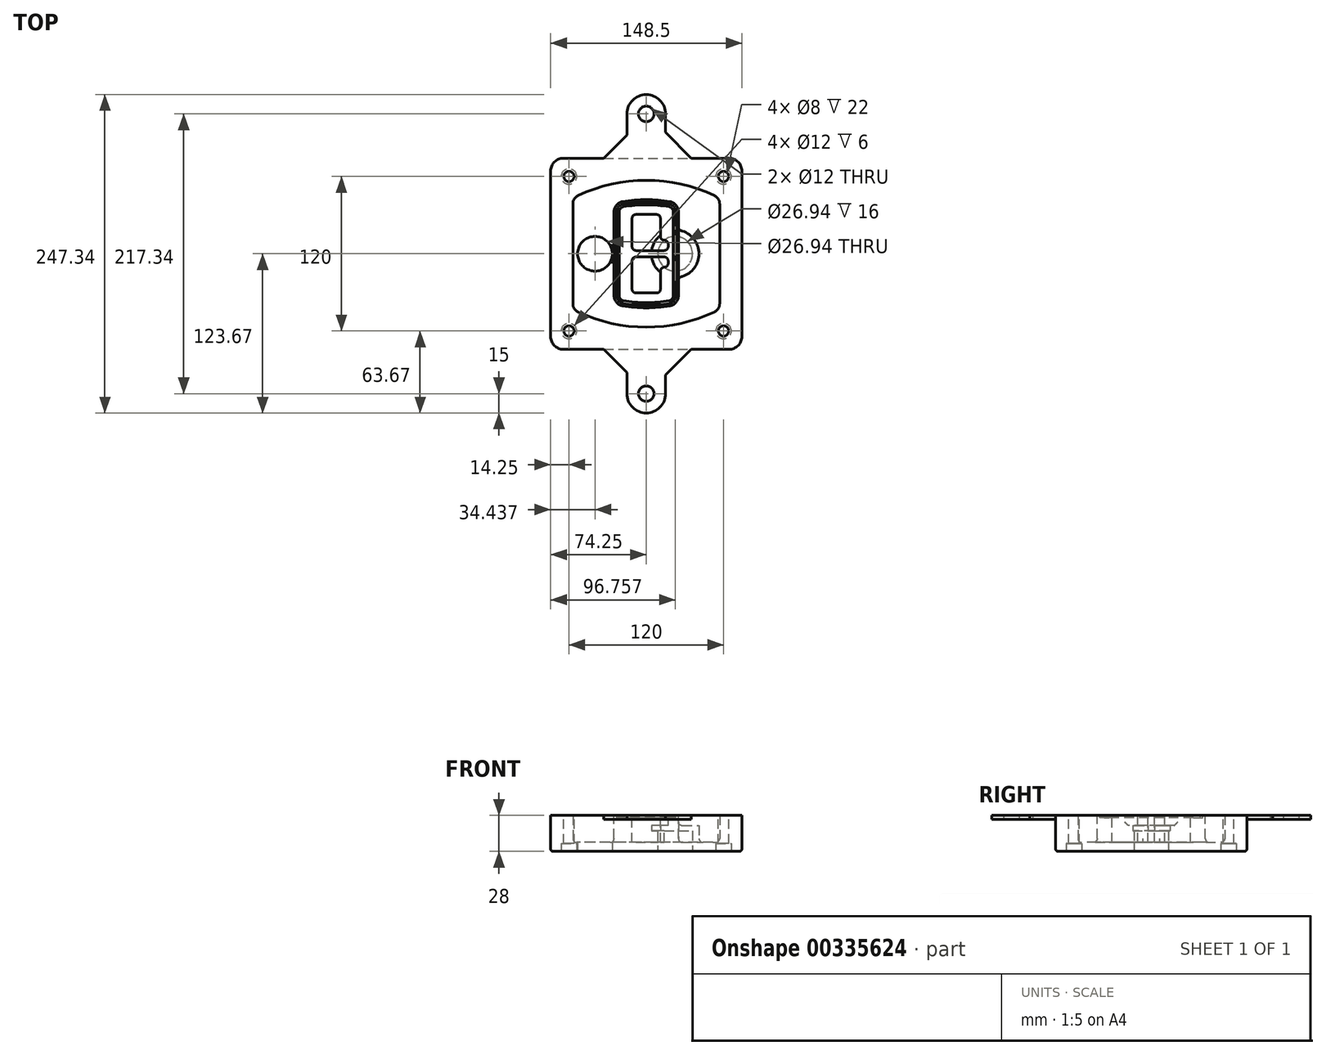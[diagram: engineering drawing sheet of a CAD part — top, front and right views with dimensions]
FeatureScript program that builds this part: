
annotation { "Feature Type Name" : "Feature", "Feature Type Description" : "" }
export const myFeature = defineFeature(function(context is Context, id is Id, definition is map)
    precondition{}
    {
        {
            var Q0;
            Q0=qCreatedBy(makeId("Top.planeOp"),FACE);
            var sketch = newSketch(context, id + "F0", { "sketchPlane" : qUnion([Q0])});
            skPoint(sketch, "E0.rect.middle", {"position": v(0, 0) * mm});
            skLineSegment(sketch, "E1.bottom", {"start": v(-64.25, -74.25) * mm, "end": v(64.25, -74.25) * mm});
            skLineSegment(sketch, "E1.top", {"start": v(-64.25, 74.25) * mm, "end": v(64.25, 74.25) * mm});
            skLineSegment(sketch, "E1.left", {"start": v(-74.25, -64.25) * mm, "end": v(-74.25, 64.25) * mm});
            skLineSegment(sketch, "E1.right", {"start": v(74.25, -64.25) * mm, "end": v(74.25, 64.25) * mm});
            skLineSegment(sketch, "E2", {"start": v(-74.25, 74.25) * mm, "end": v(74.25, -74.25) * mm, "construction": true});
            skLineSegment(sketch, "E3", {"start": v(74.25, 74.25) * mm, "end": v(-74.25, -74.25) * mm, "construction": true});
            skCircle(sketch, "E4", {"center": v(-60, 60) * mm, "radius": 4 * mm});
            skCircle(sketch, "E5", {"center": v(60, 60) * mm, "radius": 4 * mm});
            skCircle(sketch, "E6", {"center": v(60, -60) * mm, "radius": 4 * mm});
            skCircle(sketch, "E7", {"center": v(-60, -60) * mm, "radius": 4 * mm});
            skLineSegment(sketch, "E8", {"start": v(-60, 60) * mm, "end": v(60, 60) * mm, "construction": true});
            skLineSegment(sketch, "E9", {"start": v(60, 60) * mm, "end": v(60, -60) * mm, "construction": true});
            skLineSegment(sketch, "E10", {"start": v(60, -60) * mm, "end": v(-60, -60) * mm, "construction": true});
            skLineSegment(sketch, "E11", {"start": v(-60, -60) * mm, "end": v(-60, 60) * mm, "construction": true});
            skLineSegment(sketch, "E12", {"start": v(-60, 38.83) * mm, "end": v(-60, -38.83) * mm});
            skLineSegment(sketch, "E13", {"start": v(60, 38.83) * mm, "end": v(60, -38.83) * mm});
            skArc(sketch, "E14", {"start": v(54.26, 47.88) * mm, "mid": v(0, 60) * mm, "end": v(-54.26, 47.88) * mm});
            skArc(sketch, "E15", {"start": v(-54.26, -47.88) * mm, "mid": v(0, -60) * mm, "end": v(54.26, -47.88) * mm});
            skLineSegment(sketch, "E16", {"start": v(-60, 0) * mm, "end": v(60, 0) * mm, "construction": true});
            skPoint(sketch, "E17.visualSharp", {"position": v(-60, -45) * mm});
            skArc(sketch, "E17.filletArc", {"start": v(-60, -38.83) * mm, "mid": v(-58.44, -44.2) * mm, "end": v(-54.26, -47.88) * mm});
            skPoint(sketch, "E18.visualSharp", {"position": v(-60, 45) * mm});
            skArc(sketch, "E18.filletArc", {"start": v(-54.26, 47.88) * mm, "mid": v(-58.44, 44.2) * mm, "end": v(-60, 38.83) * mm});
            skPoint(sketch, "E19.visualSharp", {"position": v(60, 45) * mm});
            skArc(sketch, "E19.filletArc", {"start": v(60, 38.83) * mm, "mid": v(58.44, 44.2) * mm, "end": v(54.26, 47.88) * mm});
            skPoint(sketch, "E20.visualSharp", {"position": v(60, -45) * mm});
            skArc(sketch, "E20.filletArc", {"start": v(54.26, -47.88) * mm, "mid": v(58.44, -44.2) * mm, "end": v(60, -38.83) * mm});
            skPoint(sketch, "E21.visualSharp", {"position": v(-74.25, 74.25) * mm});
            skArc(sketch, "E21.filletArc", {"start": v(-64.25, 74.25) * mm, "mid": v(-71.32, 71.32) * mm, "end": v(-74.25, 64.25) * mm});
            skPoint(sketch, "E22.visualSharp", {"position": v(74.25, 74.25) * mm});
            skArc(sketch, "E22.filletArc", {"start": v(74.25, 64.25) * mm, "mid": v(71.32, 71.32) * mm, "end": v(64.25, 74.25) * mm});
            skPoint(sketch, "E23.visualSharp", {"position": v(74.25, -74.25) * mm});
            skArc(sketch, "E23.filletArc", {"start": v(64.25, -74.25) * mm, "mid": v(71.32, -71.32) * mm, "end": v(74.25, -64.25) * mm});
            skPoint(sketch, "E24.visualSharp", {"position": v(-74.25, -74.25) * mm});
            skArc(sketch, "E24.filletArc", {"start": v(-74.25, -64.25) * mm, "mid": v(-71.32, -71.32) * mm, "end": v(-64.25, -74.25) * mm});
            skArc(sketch, "E25.0", {"start": v(57, 38.83) * mm, "mid": v(55.9, 42.58) * mm, "end": v(52.98, 45.17) * mm});
            skLineSegment(sketch, "E25.1", {"start": v(57, 38.83) * mm, "end": v(57, -38.83) * mm});
            skArc(sketch, "E25.2", {"start": v(52.98, -45.17) * mm, "mid": v(55.9, -42.58) * mm, "end": v(57, -38.83) * mm});
            skArc(sketch, "E25.3", {"start": v(-52.98, -45.17) * mm, "mid": v(0, -57) * mm, "end": v(52.98, -45.17) * mm});
            skArc(sketch, "E25.4", {"start": v(-57, -38.83) * mm, "mid": v(-55.9, -42.58) * mm, "end": v(-52.98, -45.17) * mm});
            skArc(sketch, "E25.5", {"start": v(52.98, 45.17) * mm, "mid": v(0, 57) * mm, "end": v(-52.98, 45.17) * mm});
            skLineSegment(sketch, "E25.6", {"start": v(-57, 38.83) * mm, "end": v(-57, -38.83) * mm});
            skArc(sketch, "E25.7", {"start": v(-52.98, 45.17) * mm, "mid": v(-55.9, 42.58) * mm, "end": v(-57, 38.83) * mm});
            skArc(sketch, "E26.0", {"start": v(-55.96, 51.5) * mm, "mid": v(-61.82, 46.33) * mm, "end": v(-64, 38.83) * mm});
            skArc(sketch, "E26.1", {"start": v(55.96, 51.5) * mm, "mid": v(0, 64) * mm, "end": v(-55.96, 51.5) * mm});
            skArc(sketch, "E26.2", {"start": v(64, 38.83) * mm, "mid": v(61.82, 46.33) * mm, "end": v(55.96, 51.5) * mm});
            skLineSegment(sketch, "E26.3", {"start": v(64, 38.83) * mm, "end": v(64, -38.83) * mm});
            skArc(sketch, "E26.4", {"start": v(55.96, -51.5) * mm, "mid": v(61.82, -46.33) * mm, "end": v(64, -38.83) * mm});
            skLineSegment(sketch, "E26.5", {"start": v(-64, 38.83) * mm, "end": v(-64, -38.83) * mm});
            skArc(sketch, "E26.6", {"start": v(-55.96, -51.5) * mm, "mid": v(0, -64) * mm, "end": v(55.96, -51.5) * mm});
            skArc(sketch, "E26.7", {"start": v(-64, -38.83) * mm, "mid": v(-61.82, -46.33) * mm, "end": v(-55.96, -51.5) * mm});
            skSolve(sketch);
        }
        {
            var Q0;
            Q0=makeQuery(id+"F0.imprint","IMPRINT",FACE,{"disambiguationData":[TD([[makeQuery(id+"F0.imprint","IMPRINT",EDGE,{"derivedFrom":sQuery(id+"F0.wireOp",EDGE,"E1.bottom")}),1.0]])]});
            var Q1;
            Q1=makeQuery(id+"F0.imprint","IMPRINT",FACE,{"disambiguationData":[TD([[makeQuery(id+"F0.imprint","IMPRINT",EDGE,{"derivedFrom":sQuery(id+"F0.wireOp",EDGE,"E12")}),1.0]])]});
            var Q2;
            Q2=makeQuery(id+"F0.imprint","IMPRINT",FACE,{"disambiguationData":[TD([[makeQuery(id+"F0.imprint","IMPRINT",EDGE,{"derivedFrom":sQuery(id+"F0.wireOp",EDGE,"E25.0")}),1.0]])]});
            var Q3;
            Q3=makeQuery(id+"F0.imprint","IMPRINT",FACE,{"disambiguationData":[TD([[makeQuery(id+"F0.imprint","IMPRINT",EDGE,{"derivedFrom":sQuery(id+"F0.wireOp",EDGE,"E12")}),-1.0]])]});
            extrude(context, id + "F1", {"entities" : qUnion([Q0, Q1, Q2, Q3]), "oppositeDirection" : true, "depth" : 25 * mm});
        }
        {
            var Q0;
            Q0=makeQuery(id+"F0.imprint","IMPRINT",FACE,{"disambiguationData":[TD([[makeQuery(id+"F0.imprint","IMPRINT",EDGE,{"derivedFrom":sQuery(id+"F0.wireOp",EDGE,"E12")}),1.0]])]});
            extrude(context, id + "F2", {"entities" : qUnion([Q0]), "operationType" : NewBodyOperationType.ADD, "depth" : 3 * mm});
        }
        {
            var Q0;
            Q0=makeQuery(id+"F0.imprint","IMPRINT",FACE,{"disambiguationData":[TD([[makeQuery(id+"F0.imprint","IMPRINT",EDGE,{"derivedFrom":sQuery(id+"F0.wireOp",EDGE,"E25.0")}),1.0]])]});
            extrude(context, id + "F3", {"entities" : qUnion([Q0]), "operationType" : NewBodyOperationType.REMOVE, "oppositeDirection" : true, "depth" : 18 * mm});
        }
        {
            var Q0;
            Q0=makeQuery(id+"F2.opExtrude","CAP_FACE",FACE,{"disambiguationData":[OSD([sQuery(id+"F0.wireOp",EDGE,"E12"),sQuery(id+"F0.wireOp",EDGE,"E13"),sQuery(id+"F0.wireOp",EDGE,"E14"),sQuery(id+"F0.wireOp",EDGE,"E15"),sQuery(id+"F0.wireOp",EDGE,"E17.filletArc"),sQuery(id+"F0.wireOp",EDGE,"E18.filletArc"),sQuery(id+"F0.wireOp",EDGE,"E19.filletArc"),sQuery(id+"F0.wireOp",EDGE,"E20.filletArc"),sQuery(id+"F0.wireOp",EDGE,"E25.0"),sQuery(id+"F0.wireOp",EDGE,"E25.1"),sQuery(id+"F0.wireOp",EDGE,"E25.2"),sQuery(id+"F0.wireOp",EDGE,"E25.3"),sQuery(id+"F0.wireOp",EDGE,"E25.4"),sQuery(id+"F0.wireOp",EDGE,"E25.5"),sQuery(id+"F0.wireOp",EDGE,"E25.6"),sQuery(id+"F0.wireOp",EDGE,"E25.7")])],"isStart":false});
            var sketch = newSketch(context, id + "F4", { "sketchPlane" : qUnion([Q0])});
            skArc(sketch, "E27.0", {"start": v(-18.34, -40.45) * mm, "mid": v(0, -42) * mm, "end": v(18.34, -40.45) * mm});
            skArc(sketch, "E28.0", {"start": v(18.34, 40.45) * mm, "mid": v(0, 42) * mm, "end": v(-18.34, 40.45) * mm});
            skLineSegment(sketch, "E29", {"start": v(-25, 32.57) * mm, "end": v(-25, -32.57) * mm});
            skLineSegment(sketch, "E30", {"start": v(25, 32.57) * mm, "end": v(25, -32.57) * mm});
            skLineSegment(sketch, "E31", {"start": v(-25, 39.1) * mm, "end": v(25, 39.1) * mm, "construction": true});
            skLineSegment(sketch, "E32", {"start": v(-25, -39.1) * mm, "end": v(25, -39.1) * mm, "construction": true});
            skPoint(sketch, "E33.visualSharp", {"position": v(-25, 39.1) * mm});
            skArc(sketch, "E33.filletArc", {"start": v(-18.34, 40.45) * mm, "mid": v(-23.11, 37.73) * mm, "end": v(-25, 32.57) * mm});
            skPoint(sketch, "E34.visualSharp", {"position": v(25, 39.1) * mm});
            skArc(sketch, "E34.filletArc", {"start": v(25, 32.57) * mm, "mid": v(23.11, 37.73) * mm, "end": v(18.34, 40.45) * mm});
            skPoint(sketch, "E35.visualSharp", {"position": v(25, -39.1) * mm});
            skArc(sketch, "E35.filletArc", {"start": v(18.34, -40.45) * mm, "mid": v(23.11, -37.73) * mm, "end": v(25, -32.57) * mm});
            skPoint(sketch, "E36.visualSharp", {"position": v(-25, -39.1) * mm});
            skArc(sketch, "E36.filletArc", {"start": v(-25, -32.57) * mm, "mid": v(-23.11, -37.73) * mm, "end": v(-18.34, -40.45) * mm});
            skArc(sketch, "E37.0", {"start": v(52.98, 45.17) * mm, "mid": v(0, 57) * mm, "end": v(-52.98, 45.17) * mm});
            skArc(sketch, "E37.1", {"start": v(-52.98, 45.17) * mm, "mid": v(-55.9, 42.58) * mm, "end": v(-57, 38.83) * mm});
            skLineSegment(sketch, "E37.2", {"start": v(-57, 38.83) * mm, "end": v(-57, -38.83) * mm});
            skArc(sketch, "E37.3", {"start": v(-57, -38.83) * mm, "mid": v(-55.9, -42.58) * mm, "end": v(-52.98, -45.17) * mm});
            skArc(sketch, "E37.4", {"start": v(-52.98, -45.17) * mm, "mid": v(0, -57) * mm, "end": v(52.98, -45.17) * mm});
            skArc(sketch, "E37.5", {"start": v(52.98, -45.17) * mm, "mid": v(55.9, -42.58) * mm, "end": v(57, -38.83) * mm});
            skLineSegment(sketch, "E37.6", {"start": v(57, 38.83) * mm, "end": v(57, -38.83) * mm});
            skArc(sketch, "E37.7", {"start": v(57, 38.83) * mm, "mid": v(55.9, 42.58) * mm, "end": v(52.98, 45.17) * mm});
            skLineSegment(sketch, "E38.0", {"start": v(23, 32.57) * mm, "end": v(23, -32.57) * mm});
            skArc(sketch, "E38.1", {"start": v(18, -38.48) * mm, "mid": v(21.58, -36.44) * mm, "end": v(23, -32.57) * mm});
            skArc(sketch, "E38.2", {"start": v(-18, -38.48) * mm, "mid": v(0, -40) * mm, "end": v(18, -38.48) * mm});
            skArc(sketch, "E38.3", {"start": v(-23, -32.57) * mm, "mid": v(-21.58, -36.44) * mm, "end": v(-18, -38.48) * mm});
            skLineSegment(sketch, "E38.4", {"start": v(-23, 32.57) * mm, "end": v(-23, -32.57) * mm});
            skArc(sketch, "E38.5", {"start": v(23, 32.57) * mm, "mid": v(21.58, 36.44) * mm, "end": v(18, 38.48) * mm});
            skArc(sketch, "E38.6", {"start": v(-18, 38.48) * mm, "mid": v(-21.58, 36.44) * mm, "end": v(-23, 32.57) * mm});
            skArc(sketch, "E38.7", {"start": v(18, 38.48) * mm, "mid": v(0, 40) * mm, "end": v(-18, 38.48) * mm});
            skArc(sketch, "E39.0", {"start": v(21, 32.57) * mm, "mid": v(20.06, 35.15) * mm, "end": v(17.67, 36.5) * mm});
            skLineSegment(sketch, "E39.1", {"start": v(21, 32.57) * mm, "end": v(21, -32.57) * mm});
            skArc(sketch, "E39.2", {"start": v(17.67, -36.5) * mm, "mid": v(20.06, -35.15) * mm, "end": v(21, -32.57) * mm});
            skArc(sketch, "E39.3", {"start": v(-17.67, -36.5) * mm, "mid": v(0, -38) * mm, "end": v(17.67, -36.5) * mm});
            skArc(sketch, "E39.4", {"start": v(-21, -32.57) * mm, "mid": v(-20.06, -35.15) * mm, "end": v(-17.67, -36.5) * mm});
            skArc(sketch, "E39.5", {"start": v(17.67, 36.5) * mm, "mid": v(0, 38) * mm, "end": v(-17.67, 36.5) * mm});
            skLineSegment(sketch, "E39.6", {"start": v(-21, 32.57) * mm, "end": v(-21, -32.57) * mm});
            skArc(sketch, "E39.7", {"start": v(-17.67, 36.5) * mm, "mid": v(-20.06, 35.15) * mm, "end": v(-21, 32.57) * mm});
            skLineSegment(sketch, "E40", {"start": v(-25, 0) * mm, "end": v(25, 0) * mm, "construction": true});
            skLineSegment(sketch, "E41", {"start": v(-11, 5.5) * mm, "end": v(-11, 27.5) * mm});
            skLineSegment(sketch, "E42", {"start": v(-8, 30.5) * mm, "end": v(8, 30.5) * mm});
            skLineSegment(sketch, "E43", {"start": v(11, 27.5) * mm, "end": v(11, 13.5) * mm});
            skLineSegment(sketch, "E44", {"start": v(14, 10.5) * mm, "end": v(14, 10.5) * mm});
            skLineSegment(sketch, "E45", {"start": v(17, 7.5) * mm, "end": v(17, 5.5) * mm});
            skLineSegment(sketch, "E46", {"start": v(14, 2.5) * mm, "end": v(-8, 2.5) * mm});
            skPoint(sketch, "E47.visualSharp", {"position": v(-11, 30.5) * mm});
            skArc(sketch, "E47.filletArc", {"start": v(-8, 30.5) * mm, "mid": v(-10.12, 29.62) * mm, "end": v(-11, 27.5) * mm});
            skPoint(sketch, "E48.visualSharp", {"position": v(11, 30.5) * mm});
            skArc(sketch, "E48.filletArc", {"start": v(11, 27.5) * mm, "mid": v(10.12, 29.62) * mm, "end": v(8, 30.5) * mm});
            skPoint(sketch, "E49.visualSharp", {"position": v(11, 10.5) * mm});
            skArc(sketch, "E49.filletArc", {"start": v(11, 13.5) * mm, "mid": v(11.88, 11.38) * mm, "end": v(14, 10.5) * mm});
            skPoint(sketch, "E50.visualSharp", {"position": v(17, 10.5) * mm});
            skArc(sketch, "E50.filletArc", {"start": v(17, 7.5) * mm, "mid": v(16.12, 9.62) * mm, "end": v(14, 10.5) * mm});
            skPoint(sketch, "E51.visualSharp", {"position": v(17, 2.5) * mm});
            skArc(sketch, "E51.filletArc", {"start": v(14, 2.5) * mm, "mid": v(16.12, 3.38) * mm, "end": v(17, 5.5) * mm});
            skPoint(sketch, "E52.visualSharp", {"position": v(-11, 2.5) * mm});
            skArc(sketch, "E52.filletArc", {"start": v(-11, 5.5) * mm, "mid": v(-10.12, 3.38) * mm, "end": v(-8, 2.5) * mm});
            skLineSegment(sketch, "E53.0.MirrorCS", {"start": v(14, -2.5) * mm, "end": v(-8, -2.5) * mm});
            skArc(sketch, "E54.0.MirrorCS", {"start": v(-11, -5.5) * mm, "mid": v(-10.12, -3.38) * mm, "end": v(-8, -2.5) * mm});
            skLineSegment(sketch, "E55.0.MirrorCS", {"start": v(-11, -5.5) * mm, "end": v(-11, -27.5) * mm});
            skArc(sketch, "E56.0.MirrorCS", {"start": v(-8, -30.5) * mm, "mid": v(-10.12, -29.62) * mm, "end": v(-11, -27.5) * mm});
            skLineSegment(sketch, "E57.0.MirrorCS", {"start": v(-8, -30.5) * mm, "end": v(8, -30.5) * mm});
            skArc(sketch, "E58.0.MirrorCS", {"start": v(11, -27.5) * mm, "mid": v(10.12, -29.62) * mm, "end": v(8, -30.5) * mm});
            skLineSegment(sketch, "E59.0.MirrorCS", {"start": v(11, -27.5) * mm, "end": v(11, -13.5) * mm});
            skArc(sketch, "E60.0.MirrorCS", {"start": v(11, -13.5) * mm, "mid": v(11.88, -11.38) * mm, "end": v(14, -10.5) * mm});
            skArc(sketch, "E61.0.MirrorCS", {"start": v(17, -7.5) * mm, "mid": v(16.12, -9.62) * mm, "end": v(14, -10.5) * mm});
            skLineSegment(sketch, "E62.0.MirrorCS", {"start": v(17, -7.5) * mm, "end": v(17, -5.5) * mm});
            skArc(sketch, "E63.0.MirrorCS", {"start": v(14, -2.5) * mm, "mid": v(16.12, -3.38) * mm, "end": v(17, -5.5) * mm});
            skSolve(sketch);
        }
        {
            var Q0;
            Q0=makeQuery(id+"F4.imprint","IMPRINT",FACE,{"disambiguationData":[TD([[makeQuery(id+"F4.imprint","IMPRINT",EDGE,{"derivedFrom":sQuery(id+"F4.wireOp",EDGE,"E27.0")}),1.0]])]});
            var Q1;
            Q1=makeQuery(id+"F4.imprint","IMPRINT",FACE,{"disambiguationData":[TD([[makeQuery(id+"F4.imprint","IMPRINT",EDGE,{"derivedFrom":sQuery(id+"F4.wireOp",EDGE,"E38.0")}),-1.0]])]});
            var Q2;
            Q2=makeQuery(id+"F4.imprint","IMPRINT",FACE,{"disambiguationData":[TD([[makeQuery(id+"F4.imprint","IMPRINT",EDGE,{"derivedFrom":sQuery(id+"F4.wireOp",EDGE,"E39.0")}),1.0]])]});
            extrude(context, id + "F5", {"entities" : qUnion([Q0, Q1, Q2]), "operationType" : NewBodyOperationType.ADD, "endBound" : BoundingType.UP_TO_NEXT, "oppositeDirection" : true, "depth" : 25 * mm});
        }
        {
            var Q0;
            Q0=makeQuery(id+"F4.imprint","IMPRINT",FACE,{"disambiguationData":[TD([[makeQuery(id+"F4.imprint","IMPRINT",EDGE,{"derivedFrom":sQuery(id+"F4.wireOp",EDGE,"E38.0")}),-1.0]])]});
            extrude(context, id + "F6", {"entities" : qUnion([Q0]), "operationType" : NewBodyOperationType.REMOVE, "oppositeDirection" : true, "depth" : 2 * mm});
        }
        {
            var Q0;
            Q0=makeQuery(id+"F1.opExtrude","CAP_FACE",FACE,{"disambiguationData":[OSD([sQuery(id+"F0.wireOp",EDGE,"E1.bottom"),sQuery(id+"F0.wireOp",EDGE,"E1.top"),sQuery(id+"F0.wireOp",EDGE,"E1.left"),sQuery(id+"F0.wireOp",EDGE,"E1.right"),sQuery(id+"F0.wireOp",EDGE,"E4"),sQuery(id+"F0.wireOp",EDGE,"E5"),sQuery(id+"F0.wireOp",EDGE,"E6"),sQuery(id+"F0.wireOp",EDGE,"E7"),sQuery(id+"F0.wireOp",EDGE,"E21.filletArc"),sQuery(id+"F0.wireOp",EDGE,"E22.filletArc"),sQuery(id+"F0.wireOp",EDGE,"E23.filletArc"),sQuery(id+"F0.wireOp",EDGE,"E24.filletArc")])],"isStart":false});
            var sketch = newSketch(context, id + "F7", { "sketchPlane" : qUnion([Q0])});
            skCircle(sketch, "E64", {"center": v(22.5, 0) * mm, "radius": 13.47 * mm});
            skCircle(sketch, "E65", {"center": v(-39.81, 0) * mm, "radius": 13.47 * mm});
            skLineSegment(sketch, "E66", {"start": v(74.25, 0) * mm, "end": v(-74.25, 0) * mm});
            skCircle(sketch, "E67", {"center": v(22.5, 0) * mm, "radius": 18.47 * mm});
            skCircle(sketch, "E68", {"center": v(60, -60) * mm, "radius": 6 * mm});
            skCircle(sketch, "E69", {"center": v(-60, -60) * mm, "radius": 6 * mm});
            skCircle(sketch, "E70", {"center": v(-60, 60) * mm, "radius": 6 * mm});
            skCircle(sketch, "E71", {"center": v(60, 60) * mm, "radius": 6 * mm});
            skSolve(sketch);
        }
        {
            var Q0;
            {var subQ1=sQuery(id+"F7.wireOp",EDGE,"E66");var subQ4=sQuery(id+"F7.wireOp",EDGE,"E64");var subQ6=makeQuery(id+"F7.imprint","INTERSECT",VERTEX,{"disambiguationData":[OD(0.0)],"derivedFrom":[subQ4,subQ1]});Q0=makeQuery(id+"F7.imprint","IMPRINT",FACE,{"disambiguationData":[TD([[makeQuery(id+"F7.imprint","IMPRINT",EDGE,{"disambiguationData":[TD([[subQ6,-1.0]])],"derivedFrom":subQ4}),-1.0]])]});}
            var Q1;
            {var subQ0=sQuery(id+"F7.wireOp",EDGE,"E66");var subQ1=sQuery(id+"F7.wireOp",EDGE,"E64");var subQ3=makeQuery(id+"F7.imprint","INTERSECT",VERTEX,{"disambiguationData":[OD(0.0)],"derivedFrom":[subQ1,subQ0]});Q1=makeQuery(id+"F7.imprint","IMPRINT",FACE,{"disambiguationData":[TD([[makeQuery(id+"F7.imprint","IMPRINT",EDGE,{"disambiguationData":[TD([[subQ3,-1.0]])],"derivedFrom":subQ1}),1.0]])]});}
            var Q2;
            {var subQ0=sQuery(id+"F7.wireOp",EDGE,"E66");var subQ1=sQuery(id+"F7.wireOp",EDGE,"E64");var subQ3=makeQuery(id+"F7.imprint","INTERSECT",VERTEX,{"disambiguationData":[OD(0.0)],"derivedFrom":[subQ1,subQ0]});Q2=makeQuery(id+"F7.imprint","IMPRINT",FACE,{"disambiguationData":[TD([[makeQuery(id+"F7.imprint","IMPRINT",EDGE,{"disambiguationData":[TD([[subQ3,1.0]])],"derivedFrom":subQ1}),1.0]])]});}
            var Q3;
            {var subQ1=sQuery(id+"F7.wireOp",EDGE,"E66");var subQ4=sQuery(id+"F7.wireOp",EDGE,"E64");var subQ6=makeQuery(id+"F7.imprint","INTERSECT",VERTEX,{"disambiguationData":[OD(0.0)],"derivedFrom":[subQ4,subQ1]});Q3=makeQuery(id+"F7.imprint","IMPRINT",FACE,{"disambiguationData":[TD([[makeQuery(id+"F7.imprint","IMPRINT",EDGE,{"disambiguationData":[TD([[subQ6,1.0]])],"derivedFrom":subQ4}),-1.0]])]});}
            extrude(context, id + "F8", {"entities" : qUnion([Q0, Q1, Q2, Q3]), "operationType" : NewBodyOperationType.ADD, "oppositeDirection" : true, "depth" : 20 * mm});
        }
        {
            var Q0;
            {var subQ0=sQuery(id+"F7.wireOp",EDGE,"E66");var subQ1=sQuery(id+"F7.wireOp",EDGE,"E64");var subQ3=makeQuery(id+"F7.imprint","INTERSECT",VERTEX,{"disambiguationData":[OD(0.0)],"derivedFrom":[subQ1,subQ0]});Q0=makeQuery(id+"F7.imprint","IMPRINT",FACE,{"disambiguationData":[TD([[makeQuery(id+"F7.imprint","IMPRINT",EDGE,{"disambiguationData":[TD([[subQ3,-1.0]])],"derivedFrom":subQ1}),1.0]])]});}
            var Q1;
            {var subQ0=sQuery(id+"F7.wireOp",EDGE,"E66");var subQ1=sQuery(id+"F7.wireOp",EDGE,"E64");var subQ3=makeQuery(id+"F7.imprint","INTERSECT",VERTEX,{"disambiguationData":[OD(0.0)],"derivedFrom":[subQ1,subQ0]});Q1=makeQuery(id+"F7.imprint","IMPRINT",FACE,{"disambiguationData":[TD([[makeQuery(id+"F7.imprint","IMPRINT",EDGE,{"disambiguationData":[TD([[subQ3,1.0]])],"derivedFrom":subQ1}),1.0]])]});}
            extrude(context, id + "F9", {"entities" : qUnion([Q0, Q1]), "operationType" : NewBodyOperationType.REMOVE, "oppositeDirection" : true, "depth" : 16 * mm});
        }
        {
            var Q0;
            {var subQ0=sQuery(id+"F7.wireOp",EDGE,"E66");var subQ1=sQuery(id+"F7.wireOp",EDGE,"E65");var subQ3=makeQuery(id+"F7.imprint","INTERSECT",VERTEX,{"disambiguationData":[OD(0.0)],"derivedFrom":[subQ1,subQ0]});Q0=makeQuery(id+"F7.imprint","IMPRINT",FACE,{"disambiguationData":[TD([[makeQuery(id+"F7.imprint","IMPRINT",EDGE,{"disambiguationData":[TD([[subQ3,-1.0]])],"derivedFrom":subQ1}),1.0]])]});}
            var Q1;
            {var subQ0=sQuery(id+"F7.wireOp",EDGE,"E66");var subQ1=sQuery(id+"F7.wireOp",EDGE,"E65");var subQ3=makeQuery(id+"F7.imprint","INTERSECT",VERTEX,{"disambiguationData":[OD(0.0)],"derivedFrom":[subQ1,subQ0]});Q1=makeQuery(id+"F7.imprint","IMPRINT",FACE,{"disambiguationData":[TD([[makeQuery(id+"F7.imprint","IMPRINT",EDGE,{"disambiguationData":[TD([[subQ3,1.0]])],"derivedFrom":subQ1}),1.0]])]});}
            extrude(context, id + "F10", {"entities" : qUnion([Q0, Q1]), "operationType" : NewBodyOperationType.REMOVE, "oppositeDirection" : true, "depth" : 25 * mm});
        }
        {
            var Q0;
            Q0=makeQuery(id+"F7.imprint","IMPRINT",FACE,{"disambiguationData":[TD([[makeQuery(id+"F7.imprint","IMPRINT",EDGE,{"derivedFrom":sQuery(id+"F7.wireOp",EDGE,"E68")}),1.0]])]});
            var Q1;
            Q1=makeQuery(id+"F7.imprint","IMPRINT",FACE,{"disambiguationData":[TD([[makeQuery(id+"F7.imprint","IMPRINT",EDGE,{"derivedFrom":makeQuery(id+"F1.opExtrude","CAP_EDGE",EDGE,{"disambiguationData":[OSD([sQuery(id+"F0.wireOp",EDGE,"E5")])],"isStart":false})}),-1.0]])]});
            var Q2;
            Q2=makeQuery(id+"F7.imprint","IMPRINT",FACE,{"disambiguationData":[TD([[makeQuery(id+"F7.imprint","IMPRINT",EDGE,{"derivedFrom":sQuery(id+"F7.wireOp",EDGE,"E69")}),1.0]])]});
            var Q3;
            Q3=makeQuery(id+"F7.imprint","IMPRINT",FACE,{"disambiguationData":[TD([[makeQuery(id+"F7.imprint","IMPRINT",EDGE,{"derivedFrom":makeQuery(id+"F1.opExtrude","CAP_EDGE",EDGE,{"disambiguationData":[OSD([sQuery(id+"F0.wireOp",EDGE,"E4")])],"isStart":false})}),-1.0]])]});
            var Q4;
            Q4=makeQuery(id+"F7.imprint","IMPRINT",FACE,{"disambiguationData":[TD([[makeQuery(id+"F7.imprint","IMPRINT",EDGE,{"derivedFrom":sQuery(id+"F7.wireOp",EDGE,"E70")}),1.0]])]});
            var Q5;
            Q5=makeQuery(id+"F7.imprint","IMPRINT",FACE,{"disambiguationData":[TD([[makeQuery(id+"F7.imprint","IMPRINT",EDGE,{"derivedFrom":makeQuery(id+"F1.opExtrude","CAP_EDGE",EDGE,{"disambiguationData":[OSD([sQuery(id+"F0.wireOp",EDGE,"E7")])],"isStart":false})}),-1.0]])]});
            var Q6;
            Q6=makeQuery(id+"F7.imprint","IMPRINT",FACE,{"disambiguationData":[TD([[makeQuery(id+"F7.imprint","IMPRINT",EDGE,{"derivedFrom":sQuery(id+"F7.wireOp",EDGE,"E71")}),1.0]])]});
            var Q7;
            Q7=makeQuery(id+"F7.imprint","IMPRINT",FACE,{"disambiguationData":[TD([[makeQuery(id+"F7.imprint","IMPRINT",EDGE,{"derivedFrom":makeQuery(id+"F1.opExtrude","CAP_EDGE",EDGE,{"disambiguationData":[OSD([sQuery(id+"F0.wireOp",EDGE,"E6")])],"isStart":false})}),-1.0]])]});
            extrude(context, id + "F11", {"entities" : qUnion([Q0, Q1, Q2, Q3, Q4, Q5, Q6, Q7]), "operationType" : NewBodyOperationType.REMOVE, "oppositeDirection" : true, "depth" : 6 * mm});
        }
        {
            var Q0;
            Q0=makeQuery(id+"F9.boolean.opBoolean","COPY",FACE,{"derivedFrom":makeQuery(id+"F9.opExtrude","CAP_FACE",FACE,{"disambiguationData":[OSD([sQuery(id+"F7.wireOp",EDGE,"E64")])],"isStart":false})});
            var sketch = newSketch(context, id + "F12", { "sketchPlane" : qUnion([Q0])});
            skArc(sketch, "E72.0", {"start": v(11, 14.45) * mm, "mid": v(6.45, 9.13) * mm, "end": v(4.2, 2.5) * mm});
            skArc(sketch, "E72.1", {"start": v(4.2, -2.5) * mm, "mid": v(6.45, -9.13) * mm, "end": v(11, -14.45) * mm});
            skLineSegment(sketch, "E73", {"start": v(4.2, -2.5) * mm, "end": v(14, -2.5) * mm});
            skLineSegment(sketch, "E74.0", {"start": v(14, 2.5) * mm, "end": v(4.2, 2.5) * mm});
            skArc(sketch, "E74.1", {"start": v(14, 2.5) * mm, "mid": v(16.12, 3.38) * mm, "end": v(17, 5.5) * mm});
            skLineSegment(sketch, "E74.2", {"start": v(17, 7.5) * mm, "end": v(17, 5.5) * mm});
            skArc(sketch, "E74.3", {"start": v(17, 7.5) * mm, "mid": v(16.12, 9.62) * mm, "end": v(14, 10.5) * mm});
            skArc(sketch, "E74.4", {"start": v(11, 13.5) * mm, "mid": v(11.88, 11.38) * mm, "end": v(14, 10.5) * mm});
            skLineSegment(sketch, "E74.5", {"start": v(11, 14.45) * mm, "end": v(11, 13.5) * mm});
            skLineSegment(sketch, "E74.7", {"start": v(14, -2.5) * mm, "end": v(4.2, -2.5) * mm});
            skArc(sketch, "E74.8", {"start": v(14, -2.5) * mm, "mid": v(16.12, -3.38) * mm, "end": v(17, -5.5) * mm});
            skLineSegment(sketch, "E74.9", {"start": v(17, -7.5) * mm, "end": v(17, -5.5) * mm});
            skArc(sketch, "E74.10", {"start": v(17, -7.5) * mm, "mid": v(16.12, -9.62) * mm, "end": v(14, -10.5) * mm});
            skArc(sketch, "E74.11", {"start": v(11, -13.5) * mm, "mid": v(11.88, -11.38) * mm, "end": v(14, -10.5) * mm});
            skLineSegment(sketch, "E74.12", {"start": v(11, -14.45) * mm, "end": v(11, -13.5) * mm});
            skPoint(sketch, "E75.orphan", {"position": v(11, -27.5) * mm});
            skPoint(sketch, "E76.orphan", {"position": v(-8, -2.5) * mm});
            skPoint(sketch, "E77.orphan", {"position": v(-8, 2.5) * mm});
            skPoint(sketch, "E78.orphan", {"position": v(11, 27.5) * mm});
            skSolve(sketch);
        }
        {
            var Q0;
            {var subQ7=sQuery(id+"F12.wireOp",EDGE,"E72.0");var subQ14=sQuery(id+"F12.wireOp",EDGE,"E72.1");var subQ16=sQuery(id+"F12.wireOp",EDGE,"E74.1");var subQ18=sQuery(id+"F12.wireOp",EDGE,"E74.8");Q0=qUnion([makeQuery(id+"F12.imprint","IMPRINT",FACE,{"disambiguationData":[TD([[makeQuery(id+"F12.imprint","IMPRINT",EDGE,{"derivedFrom":subQ7}),1.0]])]}),makeQuery(id+"F12.imprint","IMPRINT",FACE,{"disambiguationData":[TD([[makeQuery(id+"F12.imprint","IMPRINT",EDGE,{"derivedFrom":subQ14}),1.0]])]}),makeQuery(id+"F12.imprint","IMPRINT",FACE,{"disambiguationData":[TD([[makeQuery(id+"F12.imprint","IMPRINT",EDGE,{"derivedFrom":subQ16}),1.0]])]}),makeQuery(id+"F12.imprint","IMPRINT",FACE,{"disambiguationData":[TD([[makeQuery(id+"F12.imprint","IMPRINT",EDGE,{"derivedFrom":subQ18}),-1.0]])]})]);}
            var Q1;
            Q1=makeQuery(id+"F5.boolean.opBoolean","SPLIT",FACE,{"disambiguationData":[TD([makeQuery(id+"F5.opExtrude","SWEPT_FACE",FACE,{"disambiguationData":[OSD([sQuery(id+"F4.wireOp",EDGE,"E41")])]})])],"derivedFrom":makeQuery(id+"F3.boolean.opBoolean","COPY",FACE,{"derivedFrom":makeQuery(id+"F3.opExtrude","CAP_FACE",FACE,{"disambiguationData":[OSD([sQuery(id+"F0.wireOp",EDGE,"E25.0"),sQuery(id+"F0.wireOp",EDGE,"E25.1"),sQuery(id+"F0.wireOp",EDGE,"E25.2"),sQuery(id+"F0.wireOp",EDGE,"E25.3"),sQuery(id+"F0.wireOp",EDGE,"E25.4"),sQuery(id+"F0.wireOp",EDGE,"E25.5"),sQuery(id+"F0.wireOp",EDGE,"E25.6"),sQuery(id+"F0.wireOp",EDGE,"E25.7")])],"isStart":false})})});
            extrude(context, id + "F13", {"entities" : qUnion([Q0]), "operationType" : NewBodyOperationType.REMOVE, "endBound" : BoundingType.UP_TO_SURFACE, "endBoundEntityFace" : qUnion([Q1]), "depth" : 25 * mm});
        }
        {
            var Q0;
            Q0=makeQuery(id+"F3.boolean.opBoolean","COPY",EDGE,{"derivedFrom":makeQuery(id+"F3.opExtrude","CAP_EDGE",EDGE,{"disambiguationData":[OSD([sQuery(id+"F0.wireOp",EDGE,"E25.6")])],"isStart":false})});
            var Q1;
            Q1=makeQuery(id+"F8.boolean.opBoolean","INTERSECT",EDGE,{"derivedFrom":[makeQuery(id+"F5.opExtrude","SWEPT_FACE",FACE,{"disambiguationData":[OSD([sQuery(id+"F4.wireOp",EDGE,"E30")])]}),makeQuery(id+"F8.opExtrude","CAP_FACE",FACE,{"disambiguationData":[OSD([sQuery(id+"F7.wireOp",EDGE,"E67")])],"isStart":false})]});
            var Q2;
            Q2=makeQuery(id+"F8.boolean.opBoolean","INTERSECT",EDGE,{"disambiguationData":[OD(1.0)],"derivedFrom":[makeQuery(id+"F5.opExtrude","SWEPT_FACE",FACE,{"disambiguationData":[OSD([sQuery(id+"F4.wireOp",EDGE,"E30")])]}),makeQuery(id+"F8.opExtrude","SWEPT_FACE",FACE,{"disambiguationData":[OSD([sQuery(id+"F7.wireOp",EDGE,"E67")])]})]});
            var Q3;
            {var subQ0=sQuery(id+"F4.wireOp",EDGE,"E30");Q3=makeQuery(id+"F8.boolean.opBoolean","SPLIT",EDGE,{"disambiguationData":[TD([makeQuery(id+"F5.opExtrude","SWEPT_FACE",FACE,{"disambiguationData":[OSD([sQuery(id+"F4.wireOp",EDGE,"E35.filletArc")])]})])],"derivedFrom":makeQuery(id+"F5.opExtrude","CAP_EDGE",EDGE,{"disambiguationData":[OSD([subQ0])],"isStart":false})});}
            var Q4;
            {var subQ0=sQuery(id+"F0.wireOp",EDGE,"E25.7");var subQ1=sQuery(id+"F0.wireOp",EDGE,"E25.1");var subQ2=sQuery(id+"F0.wireOp",EDGE,"E25.6");var subQ3=sQuery(id+"F0.wireOp",EDGE,"E25.5");var subQ4=sQuery(id+"F0.wireOp",EDGE,"E25.4");var subQ5=sQuery(id+"F0.wireOp",EDGE,"E25.0");var subQ6=sQuery(id+"F0.wireOp",EDGE,"E25.2");var subQ7=sQuery(id+"F0.wireOp",EDGE,"E25.3");Q4=makeQuery(id+"F8.boolean.opBoolean","INTERSECT",EDGE,{"derivedFrom":[makeQuery(id+"F5.boolean.opBoolean","SPLIT",FACE,{"disambiguationData":[TD([makeQuery(id+"F2.opExtrude","SWEPT_FACE",FACE,{"disambiguationData":[OSD([subQ5])]})])],"derivedFrom":makeQuery(id+"F3.boolean.opBoolean","COPY",FACE,{"derivedFrom":makeQuery(id+"F3.opExtrude","CAP_FACE",FACE,{"disambiguationData":[OSD([subQ5,subQ1,subQ6,subQ7,subQ4,subQ3,subQ2,subQ0])],"isStart":false})})}),makeQuery(id+"F8.opExtrude","SWEPT_FACE",FACE,{"disambiguationData":[OSD([sQuery(id+"F7.wireOp",EDGE,"E67")])]})]});}
            var Q5;
            Q5=makeQuery(id+"F8.boolean.opBoolean","INTERSECT",EDGE,{"disambiguationData":[OD(0.0)],"derivedFrom":[makeQuery(id+"F5.opExtrude","SWEPT_FACE",FACE,{"disambiguationData":[OSD([sQuery(id+"F4.wireOp",EDGE,"E30")])]}),makeQuery(id+"F8.opExtrude","SWEPT_FACE",FACE,{"disambiguationData":[OSD([sQuery(id+"F7.wireOp",EDGE,"E67")])]})]});
            fillet(context, id + "F14", {"entities" : qUnion([Q0, Q1, Q2, Q3, Q4, Q5]), "radius" : 3 * mm, "tangentPropagation" : true, "allowEdgeOverflow" : false});
        }
        {
            var Q0;
            Q0=makeQuery(id+"F1.opExtrude","CAP_EDGE",EDGE,{"disambiguationData":[OSD([sQuery(id+"F0.wireOp",EDGE,"E1.bottom")])],"isStart":false});
            fillet(context, id + "F15", {"entities" : qUnion([Q0]), "radius" : 2 * mm, "tangentPropagation" : true, "allowEdgeOverflow" : false});
        }
        {
            var Q0;
            {var subQ0=sQuery(id+"F0.wireOp",EDGE,"E21.filletArc");var subQ1=sQuery(id+"F0.wireOp",EDGE,"E7");var subQ2=sQuery(id+"F0.wireOp",EDGE,"E6");var subQ3=sQuery(id+"F0.wireOp",EDGE,"E5");var subQ4=sQuery(id+"F0.wireOp",EDGE,"E4");var subQ5=sQuery(id+"F0.wireOp",EDGE,"E22.filletArc");var subQ6=sQuery(id+"F0.wireOp",EDGE,"E1.bottom");var subQ7=sQuery(id+"F0.wireOp",EDGE,"E1.right");var subQ8=sQuery(id+"F0.wireOp",EDGE,"E1.top");var subQ9=sQuery(id+"F0.wireOp",EDGE,"E1.left");var subQ10=sQuery(id+"F0.wireOp",EDGE,"E23.filletArc");var subQ11=sQuery(id+"F0.wireOp",EDGE,"E24.filletArc");Q0=makeQuery(id+"F2.boolean.opBoolean","SPLIT",FACE,{"disambiguationData":[TD([makeQuery(id+"F1.opExtrude","SWEPT_FACE",FACE,{"disambiguationData":[OSD([subQ6])]})])],"derivedFrom":makeQuery(id+"F1.opExtrude","CAP_FACE",FACE,{"disambiguationData":[OSD([subQ6,subQ8,subQ9,subQ7,subQ4,subQ3,subQ2,subQ1,subQ0,subQ5,subQ10,subQ11])],"isStart":true})});}
            var sketch = newSketch(context, id + "F16", { "sketchPlane" : qUnion([Q0])});
            skLineSegment(sketch, "E79", {"start": v(-33, 74.25) * mm, "end": v(-15, 92.25) * mm});
            skLineSegment(sketch, "E80", {"start": v(35.06, 74.25) * mm, "end": v(15, 94.31) * mm});
            skLineSegment(sketch, "E81", {"start": v(15, 94.31) * mm, "end": v(15, 108.67) * mm});
            skLineSegment(sketch, "E82", {"start": v(-15, 92.25) * mm, "end": v(-15, 108.67) * mm});
            skArc(sketch, "E83", {"start": v(15, 108.67) * mm, "mid": v(0, 123.67) * mm, "end": v(-15, 108.67) * mm});
            skLineSegment(sketch, "E84", {"start": v(0, 108.67) * mm, "end": v(0, 74.25) * mm, "construction": true});
            skCircle(sketch, "E85", {"center": v(0, 108.67) * mm, "radius": 6 * mm});
            skLineSegment(sketch, "E86", {"start": v(-74.25, 0) * mm, "end": v(74.25, 0) * mm, "construction": true});
            skLineSegment(sketch, "E87.MirrorCS", {"start": v(35.06, -74.25) * mm, "end": v(15, -94.31) * mm});
            skLineSegment(sketch, "E88.MirrorCS", {"start": v(-33, -74.25) * mm, "end": v(-15, -92.25) * mm});
            skLineSegment(sketch, "E89.MirrorCS", {"start": v(0, -108.67) * mm, "end": v(0, -74.25) * mm, "construction": true});
            skCircle(sketch, "E90.MirrorC", {"center": v(0, -108.67) * mm, "radius": 6 * mm});
            skLineSegment(sketch, "E91.MirrorCS", {"start": v(-15, -92.25) * mm, "end": v(-15, -108.67) * mm});
            skLineSegment(sketch, "E92.MirrorCS", {"start": v(15, -94.31) * mm, "end": v(15, -108.67) * mm});
            skArc(sketch, "E93.MirrorCS", {"start": v(15, -108.67) * mm, "mid": v(0, -123.67) * mm, "end": v(-15, -108.67) * mm});
            skSolve(sketch);
        }
        {
            var Q0;
            {var subQ0=sQuery(id+"F16.wireOp",EDGE,"E79");Q0=makeQuery(id+"F16.imprint","IMPRINT",FACE,{"disambiguationData":[TD([[makeQuery(id+"F16.imprint","IMPRINT",EDGE,{"derivedFrom":subQ0}),-1.0]])]});}
            var Q1;
            Q1=makeQuery(id+"F16.imprint","IMPRINT",FACE,{"disambiguationData":[TD([[makeQuery(id+"F16.imprint","IMPRINT",EDGE,{"derivedFrom":makeQuery(id+"F1.opExtrude","CAP_EDGE",EDGE,{"disambiguationData":[OSD([sQuery(id+"F0.wireOp",EDGE,"E1.left")])],"isStart":true})}),-1.0]])]});
            var Q2;
            {var subQ1=sQuery(id+"F16.wireOp",EDGE,"E87.MirrorCS");Q2=makeQuery(id+"F16.imprint","IMPRINT",FACE,{"disambiguationData":[TD([[makeQuery(id+"F16.imprint","IMPRINT",EDGE,{"derivedFrom":subQ1}),-1.0]])]});}
            extrude(context, id + "F17", {"entities" : qUnion([Q0, Q1, Q2]), "operationType" : NewBodyOperationType.ADD, "depth" : 3 * mm});
        }
    });
